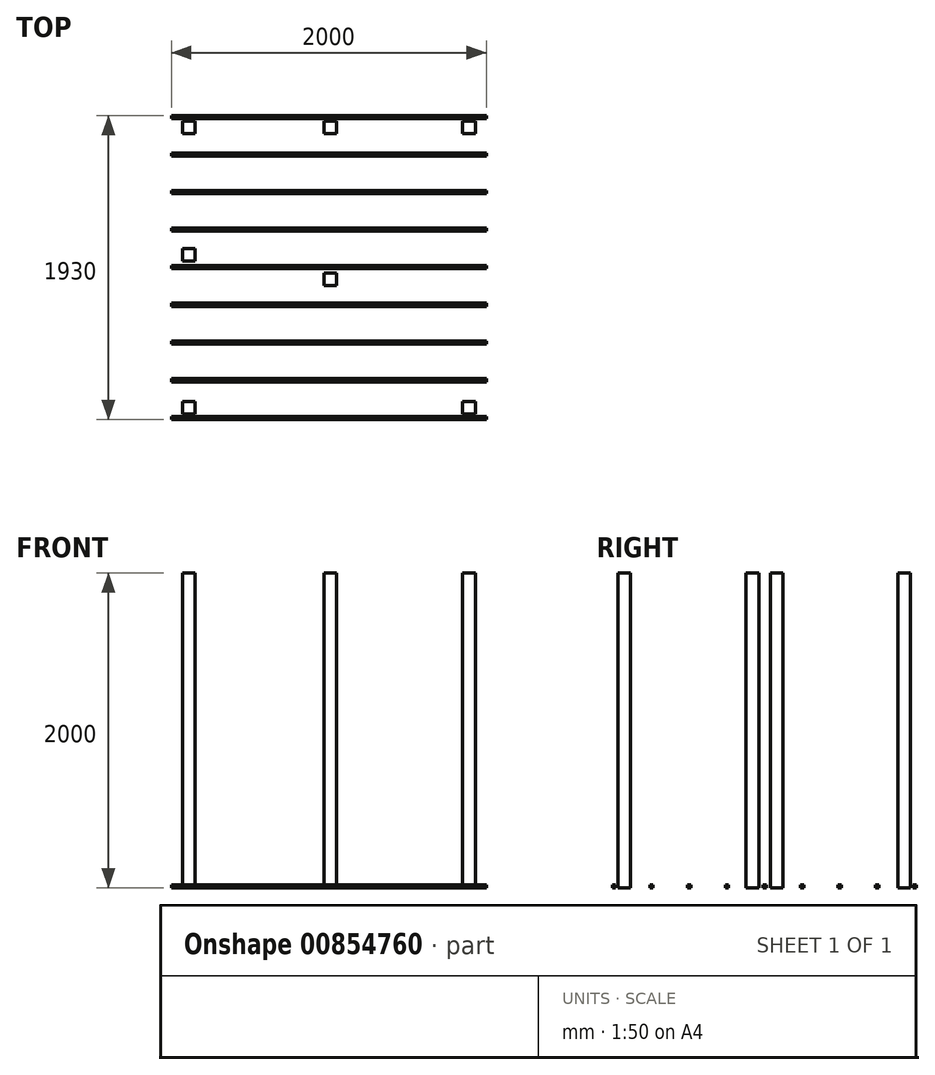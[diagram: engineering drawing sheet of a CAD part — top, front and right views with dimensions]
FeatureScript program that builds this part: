
annotation { "Feature Type Name" : "Feature", "Feature Type Description" : "" }
export const myFeature = defineFeature(function(context is Context, id is Id, definition is map)
    precondition{}
    {
        {
            var Q0;
            Q0=qCreatedBy(makeId("Top.planeOp"),FACE);
            var sketch = newSketch(context, id + "F0", { "sketchPlane" : qUnion([Q0])});
            skLineSegment(sketch, "E0.bottom", {"start": v(0, 598.73) * mm, "end": v(1860, 598.73) * mm, "construction": true});
            skLineSegment(sketch, "E0.top", {"start": v(0, -1261.27) * mm, "end": v(1860, -1261.27) * mm, "construction": true});
            skLineSegment(sketch, "E0.left", {"start": v(0, 598.73) * mm, "end": v(0, -1261.27) * mm, "construction": true});
            skLineSegment(sketch, "E0.right", {"start": v(1860, 598.73) * mm, "end": v(1860, -1261.27) * mm, "construction": true});
            skLineSegment(sketch, "E1.bottom", {"start": v(0, 598.73) * mm, "end": v(80, 598.73) * mm});
            skLineSegment(sketch, "E1.top", {"start": v(0, 518.73) * mm, "end": v(80, 518.73) * mm});
            skLineSegment(sketch, "E1.left", {"start": v(0, 598.73) * mm, "end": v(0, 518.73) * mm});
            skLineSegment(sketch, "E1.right", {"start": v(80, 598.73) * mm, "end": v(80, 518.73) * mm});
            skLineSegment(sketch, "E2.bottom", {"start": v(1860, 598.73) * mm, "end": v(1780, 598.73) * mm});
            skLineSegment(sketch, "E2.top", {"start": v(1860, 518.73) * mm, "end": v(1780, 518.73) * mm});
            skLineSegment(sketch, "E2.left", {"start": v(1860, 598.73) * mm, "end": v(1860, 518.73) * mm});
            skLineSegment(sketch, "E2.right", {"start": v(1780, 598.73) * mm, "end": v(1780, 518.73) * mm});
            skLineSegment(sketch, "E3.bottom", {"start": v(900, 598.73) * mm, "end": v(980, 598.73) * mm});
            skLineSegment(sketch, "E3.top", {"start": v(900, 518.73) * mm, "end": v(980, 518.73) * mm});
            skLineSegment(sketch, "E3.left", {"start": v(900, 598.73) * mm, "end": v(900, 518.73) * mm});
            skLineSegment(sketch, "E3.right", {"start": v(980, 598.73) * mm, "end": v(980, 518.73) * mm});
            skLineSegment(sketch, "E4.bottom", {"start": v(0, -1261.27) * mm, "end": v(80, -1261.27) * mm});
            skLineSegment(sketch, "E4.top", {"start": v(0, -1181.27) * mm, "end": v(80, -1181.27) * mm});
            skLineSegment(sketch, "E4.left", {"start": v(0, -1261.27) * mm, "end": v(0, -1181.27) * mm});
            skLineSegment(sketch, "E4.right", {"start": v(80, -1261.27) * mm, "end": v(80, -1181.27) * mm});
            skLineSegment(sketch, "E5.bottom", {"start": v(1860, -1261.27) * mm, "end": v(1780, -1261.27) * mm});
            skLineSegment(sketch, "E5.top", {"start": v(1860, -1181.27) * mm, "end": v(1780, -1181.27) * mm});
            skLineSegment(sketch, "E5.left", {"start": v(1860, -1261.27) * mm, "end": v(1860, -1181.27) * mm});
            skLineSegment(sketch, "E5.right", {"start": v(1780, -1261.27) * mm, "end": v(1780, -1181.27) * mm});
            skLineSegment(sketch, "E6.bottom", {"start": v(0, -211.27) * mm, "end": v(80, -211.27) * mm});
            skLineSegment(sketch, "E6.top", {"start": v(0, -291.27) * mm, "end": v(80, -291.27) * mm});
            skLineSegment(sketch, "E6.left", {"start": v(0, -211.27) * mm, "end": v(0, -291.27) * mm});
            skLineSegment(sketch, "E6.right", {"start": v(80, -211.27) * mm, "end": v(80, -291.27) * mm});
            skLineSegment(sketch, "E7.bottom", {"start": v(900, -366.27) * mm, "end": v(980, -366.27) * mm});
            skLineSegment(sketch, "E7.top", {"start": v(900, -446.27) * mm, "end": v(980, -446.27) * mm});
            skLineSegment(sketch, "E7.left", {"start": v(900, -366.27) * mm, "end": v(900, -446.27) * mm});
            skLineSegment(sketch, "E7.right", {"start": v(980, -366.27) * mm, "end": v(980, -446.27) * mm});
            skLineSegment(sketch, "E8", {"start": v(900, 518.73) * mm, "end": v(900, -366.27) * mm, "construction": true});
            skLineSegment(sketch, "E9", {"start": v(80, -291.27) * mm, "end": v(80, -1181.27) * mm, "construction": true});
            skLineSegment(sketch, "E10", {"start": v(80, 518.73) * mm, "end": v(900, 518.73) * mm, "construction": true});
            skSolve(sketch);
        }
        {
            var Q0;
            Q0=makeQuery(id+"F0.imprint","IMPRINT",FACE,{"disambiguationData":[TD([[makeQuery(id+"F0.imprint","IMPRINT",EDGE,{"derivedFrom":sQuery(id+"F0.wireOp",EDGE,"E3.bottom")}),-1.0]])]});
            var Q1;
            Q1=makeQuery(id+"F0.imprint","IMPRINT",FACE,{"disambiguationData":[TD([[makeQuery(id+"F0.imprint","IMPRINT",EDGE,{"derivedFrom":sQuery(id+"F0.wireOp",EDGE,"E1.bottom")}),-1.0]])]});
            var Q2;
            Q2=makeQuery(id+"F0.imprint","IMPRINT",FACE,{"disambiguationData":[TD([[makeQuery(id+"F0.imprint","IMPRINT",EDGE,{"derivedFrom":sQuery(id+"F0.wireOp",EDGE,"E6.bottom")}),-1.0]])]});
            var Q3;
            Q3=makeQuery(id+"F0.imprint","IMPRINT",FACE,{"disambiguationData":[TD([[makeQuery(id+"F0.imprint","IMPRINT",EDGE,{"derivedFrom":sQuery(id+"F0.wireOp",EDGE,"E4.bottom")}),1.0]])]});
            var Q4;
            Q4=makeQuery(id+"F0.imprint","IMPRINT",FACE,{"disambiguationData":[TD([[makeQuery(id+"F0.imprint","IMPRINT",EDGE,{"derivedFrom":sQuery(id+"F0.wireOp",EDGE,"E7.bottom")}),-1.0]])]});
            var Q5;
            Q5=makeQuery(id+"F0.imprint","IMPRINT",FACE,{"disambiguationData":[TD([[makeQuery(id+"F0.imprint","IMPRINT",EDGE,{"derivedFrom":sQuery(id+"F0.wireOp",EDGE,"E2.bottom")}),1.0]])]});
            var Q6;
            Q6=makeQuery(id+"F0.imprint","IMPRINT",FACE,{"disambiguationData":[TD([[makeQuery(id+"F0.imprint","IMPRINT",EDGE,{"derivedFrom":sQuery(id+"F0.wireOp",EDGE,"E5.bottom")}),-1.0]])]});
            extrude(context, id + "F1", {"entities" : qUnion([Q0, Q1, Q2, Q3, Q4, Q5, Q6]), "depth" : 2000 * mm, "offsetDistance" : 25 * mm});
        }
        {
            var Q0;
            Q0=qCreatedBy(makeId("Right.planeOp"),FACE);
            var sketch = newSketch(context, id + "F2", { "sketchPlane" : qUnion([Q0])});
            skLineSegment(sketch, "E11", {"start": v(-1347.39, 0) * mm, "end": v(627.6, 0) * mm, "construction": true});
            skLineSegment(sketch, "E12.bottom", {"start": v(613.73, 0) * mm, "end": v(633.73, 0) * mm});
            skLineSegment(sketch, "E12.top", {"start": v(613.73, 20) * mm, "end": v(633.73, 20) * mm});
            skLineSegment(sketch, "E12.left", {"start": v(613.73, 0) * mm, "end": v(613.73, 20) * mm});
            skLineSegment(sketch, "E12.right", {"start": v(633.73, 0) * mm, "end": v(633.73, 20) * mm});
            skLineSegment(sketch, "E13.bottom", {"start": v(395.6, 0) * mm, "end": v(375.6, 0) * mm});
            skLineSegment(sketch, "E13.top", {"start": v(395.6, 20) * mm, "end": v(375.6, 20) * mm});
            skLineSegment(sketch, "E13.left", {"start": v(395.6, 0) * mm, "end": v(395.6, 20) * mm});
            skLineSegment(sketch, "E13.right", {"start": v(375.6, 0) * mm, "end": v(375.6, 20) * mm});
            skLineSegment(sketch, "E14.bottom", {"start": v(157.48, 0) * mm, "end": v(137.48, 0) * mm});
            skLineSegment(sketch, "E14.top", {"start": v(157.48, 20) * mm, "end": v(137.48, 20) * mm});
            skLineSegment(sketch, "E14.left", {"start": v(157.48, 0) * mm, "end": v(157.48, 20) * mm});
            skLineSegment(sketch, "E14.right", {"start": v(137.48, 0) * mm, "end": v(137.48, 20) * mm});
            skLineSegment(sketch, "E15.bottom", {"start": v(-80.65, 0) * mm, "end": v(-100.65, 0) * mm});
            skLineSegment(sketch, "E15.top", {"start": v(-80.65, 20) * mm, "end": v(-100.65, 20) * mm});
            skLineSegment(sketch, "E15.left", {"start": v(-80.65, 0) * mm, "end": v(-80.65, 20) * mm});
            skLineSegment(sketch, "E15.right", {"start": v(-100.65, 0) * mm, "end": v(-100.65, 20) * mm});
            skLineSegment(sketch, "E16.bottom", {"start": v(-318.77, 0) * mm, "end": v(-338.77, 0) * mm});
            skLineSegment(sketch, "E16.top", {"start": v(-318.77, 20) * mm, "end": v(-338.77, 20) * mm});
            skLineSegment(sketch, "E16.left", {"start": v(-318.77, 0) * mm, "end": v(-318.77, 20) * mm});
            skLineSegment(sketch, "E16.right", {"start": v(-338.77, 0) * mm, "end": v(-338.77, 20) * mm});
            skLineSegment(sketch, "E17.bottom", {"start": v(-558.15, 0) * mm, "end": v(-578.15, 0) * mm});
            skLineSegment(sketch, "E17.top", {"start": v(-558.15, 20) * mm, "end": v(-578.15, 20) * mm});
            skLineSegment(sketch, "E17.left", {"start": v(-558.15, 0) * mm, "end": v(-558.15, 20) * mm});
            skLineSegment(sketch, "E17.right", {"start": v(-578.15, 0) * mm, "end": v(-578.15, 20) * mm});
            skLineSegment(sketch, "E18.bottom", {"start": v(-797.52, 0) * mm, "end": v(-817.52, 0) * mm});
            skLineSegment(sketch, "E18.top", {"start": v(-797.52, 20) * mm, "end": v(-817.52, 20) * mm});
            skLineSegment(sketch, "E18.left", {"start": v(-797.52, 0) * mm, "end": v(-797.52, 20) * mm});
            skLineSegment(sketch, "E18.right", {"start": v(-817.52, 0) * mm, "end": v(-817.52, 20) * mm});
            skLineSegment(sketch, "E19.bottom", {"start": v(-1036.9, 0) * mm, "end": v(-1056.9, 0) * mm});
            skLineSegment(sketch, "E19.top", {"start": v(-1036.9, 20) * mm, "end": v(-1056.9, 20) * mm});
            skLineSegment(sketch, "E19.left", {"start": v(-1036.9, 0) * mm, "end": v(-1036.9, 20) * mm});
            skLineSegment(sketch, "E19.right", {"start": v(-1056.9, 0) * mm, "end": v(-1056.9, 20) * mm});
            skLineSegment(sketch, "E20.bottom", {"start": v(-1276.27, 0) * mm, "end": v(-1296.27, 0) * mm});
            skLineSegment(sketch, "E20.top", {"start": v(-1276.27, 20) * mm, "end": v(-1296.27, 20) * mm});
            skLineSegment(sketch, "E20.left", {"start": v(-1276.27, 0) * mm, "end": v(-1276.27, 20) * mm});
            skLineSegment(sketch, "E20.right", {"start": v(-1296.27, 0) * mm, "end": v(-1296.27, 20) * mm});
            skLineSegment(sketch, "E21", {"start": v(-318.77, 20) * mm, "end": v(-291.27, 20) * mm, "construction": true});
            skLineSegment(sketch, "E22", {"start": v(-338.77, 20) * mm, "end": v(-366.27, 20) * mm, "construction": true});
            skLineSegment(sketch, "E23", {"start": v(-1056.9, 20) * mm, "end": v(-1276.27, 20) * mm, "construction": true});
            skLineSegment(sketch, "E24", {"start": v(-1036.9, 20) * mm, "end": v(-817.52, 20) * mm, "construction": true});
            skLineSegment(sketch, "E25", {"start": v(-578.15, 20) * mm, "end": v(-797.52, 20) * mm, "construction": true});
            skLineSegment(sketch, "E26", {"start": v(-558.15, 20) * mm, "end": v(-338.77, 20) * mm, "construction": true});
            skLineSegment(sketch, "E27", {"start": v(613.73, 20) * mm, "end": v(395.6, 20) * mm, "construction": true});
            skLineSegment(sketch, "E28", {"start": v(375.6, 20) * mm, "end": v(157.48, 20) * mm, "construction": true});
            skLineSegment(sketch, "E29", {"start": v(137.48, 20) * mm, "end": v(-80.65, 20) * mm, "construction": true});
            skLineSegment(sketch, "E30", {"start": v(-318.77, 20) * mm, "end": v(-100.65, 20) * mm, "construction": true});
            skSolve(sketch);
        }
        {
            var Q0;
            Q0=makeQuery(id+"F2.imprint","IMPRINT",FACE,{"disambiguationData":[TD([[makeQuery(id+"F2.imprint","IMPRINT",EDGE,{"derivedFrom":sQuery(id+"F2.wireOp",EDGE,"E20.bottom")}),-1.0]])]});
            var Q1;
            Q1=makeQuery(id+"F2.imprint","IMPRINT",FACE,{"disambiguationData":[TD([[makeQuery(id+"F2.imprint","IMPRINT",EDGE,{"derivedFrom":sQuery(id+"F2.wireOp",EDGE,"E19.bottom")}),-1.0]])]});
            var Q2;
            Q2=makeQuery(id+"F2.imprint","IMPRINT",FACE,{"disambiguationData":[TD([[makeQuery(id+"F2.imprint","IMPRINT",EDGE,{"derivedFrom":sQuery(id+"F2.wireOp",EDGE,"E18.bottom")}),-1.0]])]});
            var Q3;
            Q3=makeQuery(id+"F2.imprint","IMPRINT",FACE,{"disambiguationData":[TD([[makeQuery(id+"F2.imprint","IMPRINT",EDGE,{"derivedFrom":sQuery(id+"F2.wireOp",EDGE,"E17.bottom")}),-1.0]])]});
            var Q4;
            Q4=makeQuery(id+"F2.imprint","IMPRINT",FACE,{"disambiguationData":[TD([[makeQuery(id+"F2.imprint","IMPRINT",EDGE,{"derivedFrom":sQuery(id+"F2.wireOp",EDGE,"E16.bottom")}),-1.0]])]});
            var Q5;
            Q5=makeQuery(id+"F2.imprint","IMPRINT",FACE,{"disambiguationData":[TD([[makeQuery(id+"F2.imprint","IMPRINT",EDGE,{"derivedFrom":sQuery(id+"F2.wireOp",EDGE,"E15.bottom")}),-1.0]])]});
            var Q6;
            Q6=makeQuery(id+"F2.imprint","IMPRINT",FACE,{"disambiguationData":[TD([[makeQuery(id+"F2.imprint","IMPRINT",EDGE,{"derivedFrom":sQuery(id+"F2.wireOp",EDGE,"E14.bottom")}),-1.0]])]});
            var Q7;
            Q7=makeQuery(id+"F2.imprint","IMPRINT",FACE,{"disambiguationData":[TD([[makeQuery(id+"F2.imprint","IMPRINT",EDGE,{"derivedFrom":sQuery(id+"F2.wireOp",EDGE,"E13.bottom")}),-1.0]])]});
            var Q8;
            Q8=makeQuery(id+"F2.imprint","IMPRINT",FACE,{"disambiguationData":[TD([[makeQuery(id+"F2.imprint","IMPRINT",EDGE,{"derivedFrom":sQuery(id+"F2.wireOp",EDGE,"E12.bottom")}),1.0]])]});
            extrude(context, id + "F3", {"entities" : qUnion([Q0, Q1, Q2, Q3, Q4, Q5, Q6, Q7, Q8]), "depth" : 1930 * mm, "offsetDistance" : 25 * mm, "hasSecondDirection" : true, "secondDirectionOppositeDirection" : true, "secondDirectionDepth" : 70 * mm});
        }
    });
